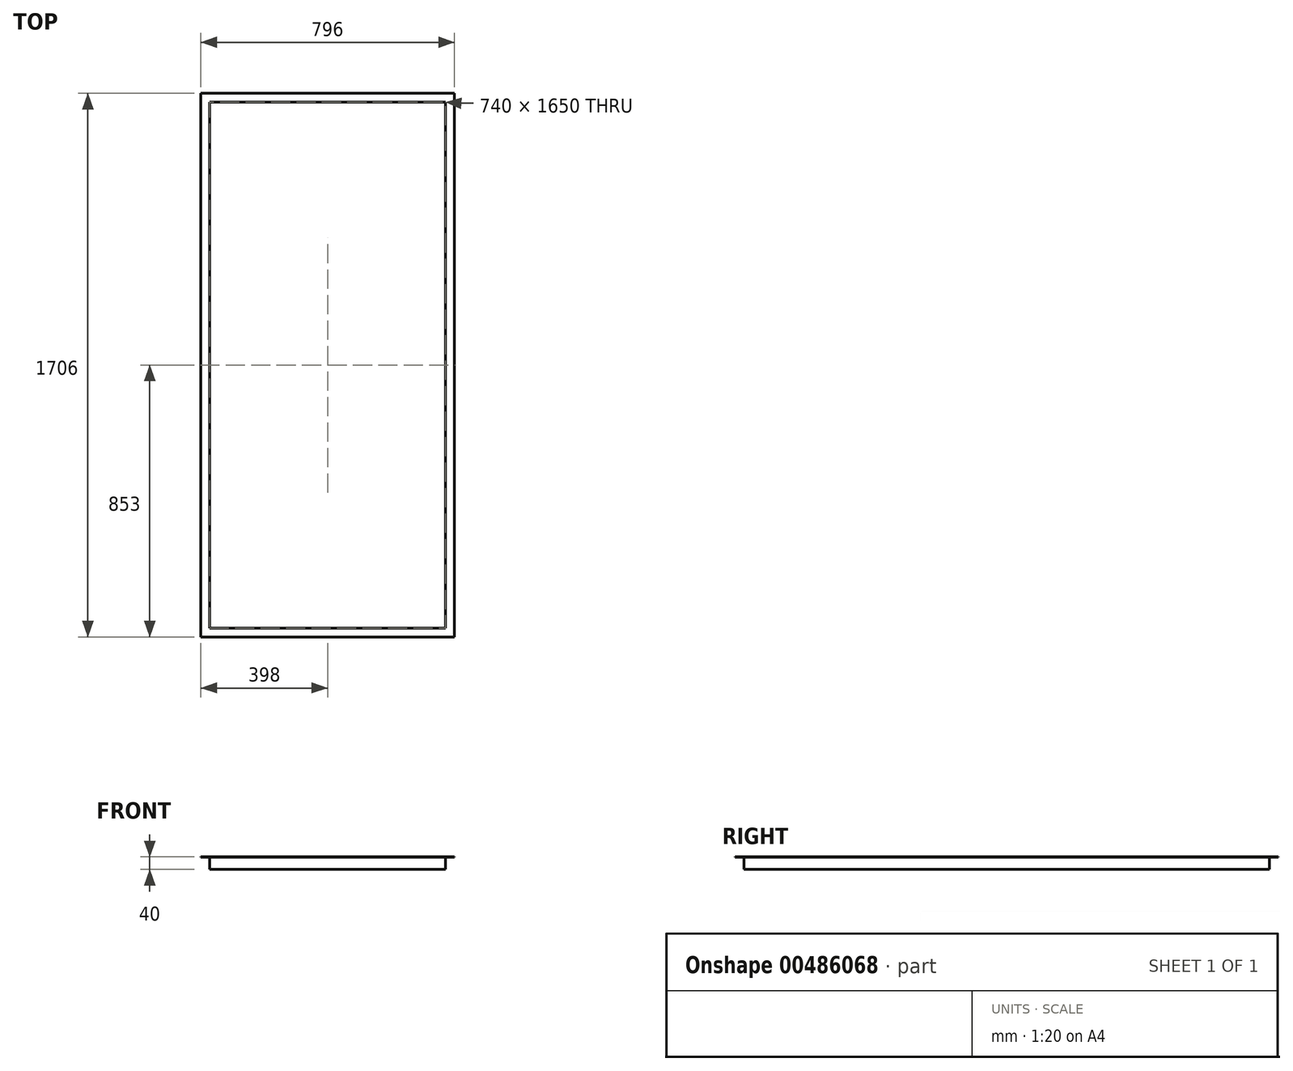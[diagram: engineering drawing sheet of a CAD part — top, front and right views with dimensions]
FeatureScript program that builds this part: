
annotation { "Feature Type Name" : "Feature", "Feature Type Description" : "" }
export const myFeature = defineFeature(function(context is Context, id is Id, definition is map)
    precondition{}
    {
        {
            var Q0;
            Q0=qCreatedBy(makeId("Top.planeOp"),FACE);
            var sketch = newSketch(context, id + "F0", { "sketchPlane" : qUnion([Q0])});
            skLineSegment(sketch, "E0.bottom", {"start": v(119.7, 99.7) * mm, "end": v(919.7, 99.7) * mm});
            skLineSegment(sketch, "E0.left", {"start": v(119.7, 99.7) * mm, "end": v(119.7, 179.7) * mm});
            skLineSegment(sketch, "E0.right", {"start": v(919.7, 99.7) * mm, "end": v(919.7, 179.7) * mm});
            skLineSegment(sketch, "E1.bottom", {"start": v(919.7, 99.7) * mm, "end": v(119.7, 99.7) * mm});
            skLineSegment(sketch, "E1.top", {"start": v(919.7, 1809.7) * mm, "end": v(119.7, 1809.7) * mm});
            skLineSegment(sketch, "E1.left", {"start": v(919.7, 99.7) * mm, "end": v(919.7, 1809.7) * mm});
            skLineSegment(sketch, "E1.right", {"start": v(119.7, 99.7) * mm, "end": v(119.7, 1809.7) * mm});
            skLineSegment(sketch, "E2.0", {"start": v(121.7, 101.7) * mm, "end": v(121.7, 1807.7) * mm});
            skLineSegment(sketch, "E2.1", {"start": v(917.7, 1807.7) * mm, "end": v(121.7, 1807.7) * mm});
            skLineSegment(sketch, "E2.2", {"start": v(917.7, 101.7) * mm, "end": v(917.7, 1807.7) * mm});
            skLineSegment(sketch, "E3.0", {"start": v(917.7, 101.7) * mm, "end": v(121.7, 101.7) * mm});
            skLineSegment(sketch, "E4.0", {"start": v(149.7, 99.7) * mm, "end": v(149.7, 101.7) * mm});
            skLineSegment(sketch, "E5.trimOffspring", {"start": v(149.7, 899.7) * mm, "end": v(149.7, 1779.7) * mm});
            skLineSegment(sketch, "E6.trimOffspring", {"start": v(149.7, 129.7) * mm, "end": v(149.7, 1779.7) * mm});
            skLineSegment(sketch, "E7.trimOffspring", {"start": v(889.7, 129.7) * mm, "end": v(149.7, 129.7) * mm});
            skLineSegment(sketch, "E8.trimOffspring", {"start": v(889.7, 129.7) * mm, "end": v(889.7, 1779.7) * mm});
            skLineSegment(sketch, "E9.trimOffspring", {"start": v(889.7, 1779.7) * mm, "end": v(149.7, 1779.7) * mm});
            skLineSegment(sketch, "E10.trimOffspring", {"start": v(889.7, 899.7) * mm, "end": v(889.7, 1779.7) * mm});
            skSolve(sketch);
        }
        {
            var Q0;
            {var subQ3=sQuery(id+"F0.wireOp",EDGE,"9af6e356-3ed3-4f5c-a46e-a3ee4cebe945.trimOffspring");Q0=makeQuery(id+"F0.imprint","IMPRINT",FACE,{"disambiguationData":[TD([[makeQuery(id+"F0.imprint","IMPRINT",EDGE,{"derivedFrom":subQ3}),-1.0]])]});}
            var Q1;
            {var subQ0=sQuery(id+"F0.wireOp",EDGE,"E5.trimOffspring");Q1=makeQuery(id+"F0.imprint","IMPRINT",FACE,{"disambiguationData":[TD([[makeQuery(id+"F0.imprint","IMPRINT",EDGE,{"derivedFrom":subQ0}),-1.0]])]});}
            var Q2;
            {var subQ0=sQuery(id+"F0.wireOp",EDGE,"9af6e356-3ed3-4f5c-a46e-a3ee4cebe945.trimOffspring");Q2=makeQuery(id+"F0.imprint","IMPRINT",FACE,{"disambiguationData":[TD([[makeQuery(id+"F0.imprint","IMPRINT",EDGE,{"derivedFrom":subQ0}),1.0]])]});}
            var Q3;
            {var subQ3=sQuery(id+"F0.wireOp",EDGE,"4a48d8a7-edd3-4a3e-b5f2-fbdc5d9baca7.0");Q3=makeQuery(id+"F0.imprint","IMPRINT",FACE,{"disambiguationData":[TD([[makeQuery(id+"F0.imprint","IMPRINT",EDGE,{"derivedFrom":subQ3}),-1.0]])]});}
            var Q4;
            {var subQ0=sQuery(id+"F0.wireOp",EDGE,"4a48d8a7-edd3-4a3e-b5f2-fbdc5d9baca7.0");Q4=makeQuery(id+"F0.imprint","IMPRINT",FACE,{"disambiguationData":[TD([[makeQuery(id+"F0.imprint","IMPRINT",EDGE,{"derivedFrom":subQ0}),1.0]])]});}
            var Q5;
            {var subQ3=sQuery(id+"F0.wireOp",EDGE,"91f4e9da-c3b3-44b5-b20d-8529f4eeb69e.0");Q5=makeQuery(id+"F0.imprint","IMPRINT",FACE,{"disambiguationData":[TD([[makeQuery(id+"F0.imprint","IMPRINT",EDGE,{"derivedFrom":subQ3}),1.0]])]});}
            var Q6;
            {var subQ0=sQuery(id+"F0.wireOp",EDGE,"E1.left");var subQ1=sQuery(id+"F0.wireOp",EDGE,"E1.bottom");var subQ2=makeQuery(id+"F0.imprint","INTERSECT",VERTEX,{"derivedFrom":[subQ1,subQ0]});Q6=makeQuery(id+"F0.imprint","IMPRINT",FACE,{"disambiguationData":[TD([[makeQuery(id+"F0.imprint","IMPRINT",EDGE,{"disambiguationData":[TD([[subQ2,-1.0]])],"derivedFrom":subQ1}),-1.0]])]});}
            var Q7;
            {var subQ3=sQuery(id+"F0.wireOp",EDGE,"207b5329-a01a-46a2-9a28-3f006c48d0ad.0");Q7=makeQuery(id+"F0.imprint","IMPRINT",FACE,{"disambiguationData":[TD([[makeQuery(id+"F0.imprint","IMPRINT",EDGE,{"derivedFrom":subQ3}),-1.0]])]});}
            var Q8;
            {var subQ0=sQuery(id+"F0.wireOp",EDGE,"207b5329-a01a-46a2-9a28-3f006c48d0ad.0");Q8=makeQuery(id+"F0.imprint","IMPRINT",FACE,{"disambiguationData":[TD([[makeQuery(id+"F0.imprint","IMPRINT",EDGE,{"derivedFrom":subQ0}),1.0]])]});}
            var Q9;
            {var subQ3=sQuery(id+"F0.wireOp",EDGE,"E4.0");Q9=makeQuery(id+"F0.imprint","IMPRINT",FACE,{"disambiguationData":[TD([[makeQuery(id+"F0.imprint","IMPRINT",EDGE,{"derivedFrom":subQ3}),1.0]])]});}
            var Q10;
            {var subQ0=sQuery(id+"F0.wireOp",EDGE,"E1.right");var subQ1=sQuery(id+"F0.wireOp",EDGE,"E1.bottom");var subQ2=makeQuery(id+"F0.imprint","INTERSECT",VERTEX,{"derivedFrom":[subQ1,subQ0]});Q10=makeQuery(id+"F0.imprint","IMPRINT",FACE,{"disambiguationData":[TD([[makeQuery(id+"F0.imprint","IMPRINT",EDGE,{"disambiguationData":[TD([[subQ2,1.0]])],"derivedFrom":subQ1}),-1.0]])]});}
            var Q11;
            {var subQ3=sQuery(id+"F0.wireOp",EDGE,"4f2842fd-9e77-4b1c-b652-776340a59b36.trimOffspring");Q11=makeQuery(id+"F0.imprint","IMPRINT",FACE,{"disambiguationData":[TD([[makeQuery(id+"F0.imprint","IMPRINT",EDGE,{"derivedFrom":subQ3}),1.0]])]});}
            extrude(context, id + "F1", {"entities" : qUnion([Q0, Q1, Q2, Q3, Q4, Q5, Q6, Q7, Q8, Q9, Q10, Q11]), "oppositeDirection" : true, "depth" : 40 * mm, "offsetDistance" : 25 * mm});
        }
        {
            var Q0;
            Q0=makeQuery(id+"F0.imprint","IMPRINT",FACE,{"disambiguationData":[TD([[makeQuery(id+"F0.imprint","IMPRINT",EDGE,{"derivedFrom":sQuery(id+"F0.wireOp",EDGE,"E6.trimOffspring")}),1.0]])]});
            extrude(context, id + "F2", {"entities" : qUnion([Q0]), "oppositeDirection" : true, "depth" : 2 * mm, "offsetDistance" : 25 * mm});
        }
    });
